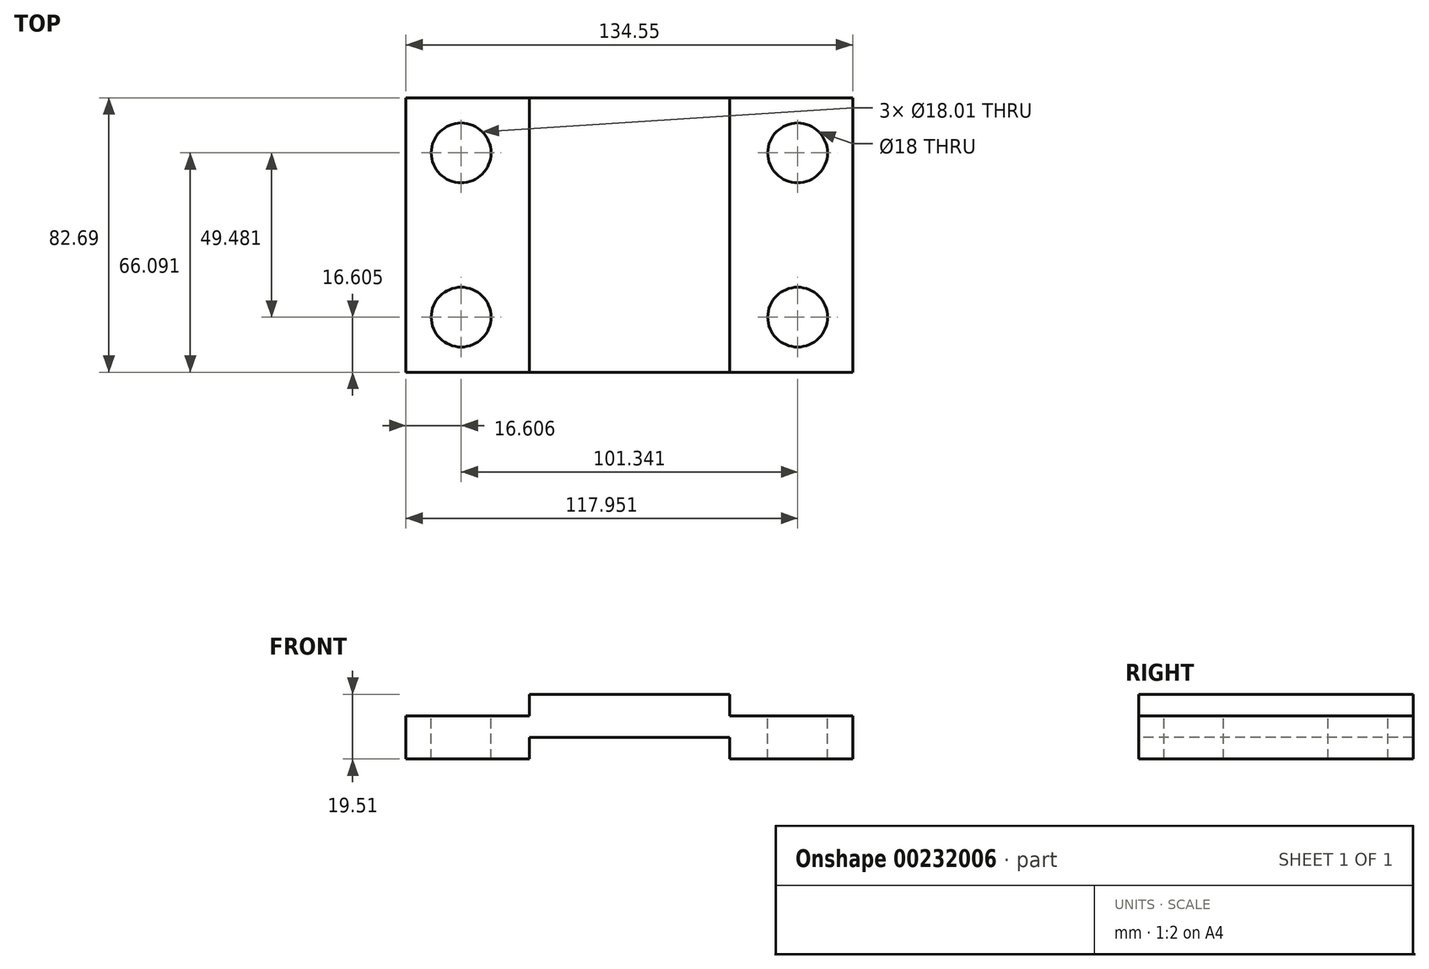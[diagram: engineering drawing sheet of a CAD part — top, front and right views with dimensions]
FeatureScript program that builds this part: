
annotation { "Feature Type Name" : "Feature", "Feature Type Description" : "" }
export const myFeature = defineFeature(function(context is Context, id is Id, definition is map)
    precondition{}
    {
        {
            var Q0;
            Q0=qCreatedBy(makeId("Top.planeOp"),FACE);
            var sketch = newSketch(context, id + "F0", { "sketchPlane" : qUnion([Q0])});
            skLineSegment(sketch, "E0.bottom", {"start": v(-90.82, 39.47) * mm, "end": v(43.73, 39.47) * mm});
            skLineSegment(sketch, "E0.top", {"start": v(-90.82, -43.22) * mm, "end": v(43.73, -43.22) * mm});
            skLineSegment(sketch, "E0.left", {"start": v(-90.82, 39.47) * mm, "end": v(-90.82, -43.22) * mm});
            skLineSegment(sketch, "E0.right", {"start": v(43.73, 39.47) * mm, "end": v(43.73, -43.22) * mm});
            skSolve(sketch);
        }
        {
            var Q0;
            Q0 = qSketchRegion(id + "F0", true);
            extrude(context, id + "F1", {"entities" : qUnion([Q0]), "depth" : 13 * mm});
        }
        {
            var Q0;
            Q0=makeQuery(id+"F1.opExtrude","SWEPT_FACE",FACE,{"disambiguationData":[OSD([sQuery(id+"F0.wireOp",EDGE,"E0.top")])]});
            var sketch = newSketch(context, id + "F2", { "sketchPlane" : qUnion([Q0])});
            skLineSegment(sketch, "E1", {"start": v(-53.73, 6.5) * mm, "end": v(-53.73, 0) * mm});
            skLineSegment(sketch, "E2", {"start": v(6.64, 6.5) * mm, "end": v(6.64, 0) * mm});
            skLineSegment(sketch, "E3", {"start": v(-53.73, 6.5) * mm, "end": v(6.64, 6.5) * mm});
            skPoint(sketch, "E4", {"position": v(-23.54, 13) * mm});
            skPoint(sketch, "E5", {"position": v(-23.54, 6.5) * mm});
            skLineSegment(sketch, "E6", {"start": v(-53.73, 0) * mm, "end": v(6.64, 0) * mm});
            skSolve(sketch);
        }
        {
            var Q0;
            Q0 = qSketchRegion(id + "F2", true);
            extrude(context, id + "F3", {"entities" : qUnion([Q0]), "operationType" : NewBodyOperationType.REMOVE, "endBound" : BoundingType.THROUGH_ALL, "oppositeDirection" : true, "depth" : 25.4 * mm});
        }
        {
            var Q0;
            Q0=makeQuery(id+"F1.opExtrude","CAP_FACE",FACE,{"disambiguationData":[OSD([sQuery(id+"F0.wireOp",EDGE,"E0.bottom"),sQuery(id+"F0.wireOp",EDGE,"E0.top"),sQuery(id+"F0.wireOp",EDGE,"E0.left"),sQuery(id+"F0.wireOp",EDGE,"E0.right")])],"isStart":false});
            var sketch = newSketch(context, id + "F4", { "sketchPlane" : qUnion([Q0])});
            skLineSegment(sketch, "E7", {"start": v(-53.73, 39.47) * mm, "end": v(-53.73, -43.22) * mm});
            skLineSegment(sketch, "E8", {"start": v(6.64, 39.47) * mm, "end": v(6.64, -43.22) * mm});
            skLineSegment(sketch, "E9", {"start": v(-53.73, 39.47) * mm, "end": v(6.64, 39.47) * mm});
            skLineSegment(sketch, "E10", {"start": v(6.64, -43.22) * mm, "end": v(-53.73, -43.22) * mm});
            skSolve(sketch);
        }
        {
            var Q0;
            Q0 = qSketchRegion(id + "F4", true);
            extrude(context, id + "F5", {"entities" : qUnion([Q0]), "operationType" : NewBodyOperationType.ADD, "depth" : 6.5 * mm});
        }
        {
            var Q0;
            {var subQ0=sQuery(id+"F0.wireOp",EDGE,"E0.right");var subQ1=sQuery(id+"F0.wireOp",EDGE,"E0.top");var subQ2=sQuery(id+"F0.wireOp",EDGE,"E0.bottom");Q0=makeQuery(id+"F5.boolean.opBoolean","SPLIT",FACE,{"disambiguationData":[TD([makeQuery(id+"F1.opExtrude","SWEPT_FACE",FACE,{"disambiguationData":[OSD([subQ0])]})])],"derivedFrom":makeQuery(id+"F1.opExtrude","CAP_FACE",FACE,{"disambiguationData":[OSD([subQ2,subQ1,sQuery(id+"F0.wireOp",EDGE,"E0.left"),subQ0])],"isStart":false})});}
            var sketch = newSketch(context, id + "F6", { "sketchPlane" : qUnion([Q0])});
            skCircle(sketch, "E11", {"center": v(27.13, 22.87) * mm, "radius": 9 * mm});
            skCircle(sketch, "E12", {"center": v(27.13, -26.61) * mm, "radius": 9 * mm});
            skCircle(sketch, "E13", {"center": v(-74.21, 22.87) * mm, "radius": 9 * mm});
            skCircle(sketch, "E14", {"center": v(-74.21, -26.61) * mm, "radius": 9 * mm});
            skSolve(sketch);
        }
        {
            var Q0;
            Q0 = qSketchRegion(id + "F6", true);
            extrude(context, id + "F7", {"entities" : qUnion([Q0]), "operationType" : NewBodyOperationType.REMOVE, "endBound" : BoundingType.THROUGH_ALL, "oppositeDirection" : true, "depth" : 25.4 * mm});
        }
    });
